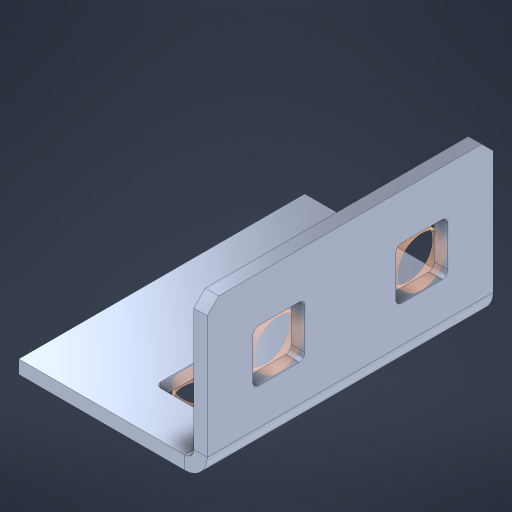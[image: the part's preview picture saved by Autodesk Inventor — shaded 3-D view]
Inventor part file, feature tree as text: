
AUTODESK INVENTOR PART (.ipt)
format: ipt  version: 2023 (Build 270158000, 158)  size: 379,392 bytes
history: native  units: in
note: dims shown in document units (in); Inventor stores cm internally (conversion verified against a paired STEP export)
features: sheet_metal_op x10, other x9, sketch x8, extrude x3, mirror x1, pattern_linear x1, chamfer x1
ambient origin geometry x8: Origin, YZ Plane, XZ Plane, XY Plane, X Axis, Y Axis, Z Axis, Center Point
bodies: Solid1 (feature_tree), Body (feature_tree)
feature tree (33):
  other  "Flange Pattern Plane"
  sheet_metal_op  "Flange Pattern"
  sheet_metal_op  "Body Pattern"
  other  "Arc Length"
  mirror  "Notch Mirror"
  pattern_linear  "Notch Pattern"  Spacing1=0.1875in  [1 undecoded]
  chamfer  "End Chamfer"
  extrude  "Half Cut"  Depth=0.0469in
  sketch  "Sketch1"  dims[d0=2.5in]
  other  "Plate1"
  sketch  "Sketch2"  dims[d1=1.0in]
  other  "Plate2"
  sheet_metal_op  "Bend1"
  sheet_metal_op  "Corner1"
  sketch  "Sketch3"  dims[d2=0.0469in]
  other  "Flange Pattern Sketch"
  sketch  "Sketch7"  dims[d3=0.0469in]
  other  "Srf1"
  other  "Srf2"
  sketch  "Sketch8"  dims[d4=0.0234in]
  sketch  "Sketch9"  dims[d5=0.0938in]
  other  "Srf91"
  sheet_metal_op  "Body Pattern Sketch"
  other  "Srf92"
  sketch  "Sketch13"  dims[d6=0.0469in]
  sketch  "Sketch14"  dims[d7=0.5in d8=90.0deg d9=0.0312in d10=0.1875in d11=0.0469in d12=0.0469in d16=0.182in d17=0.02in d18=0.0469in d19=0.0in d20=0.25in d21=0.25in d46=0.172in d47=1.0in d48=0.0in d49=0.182in d50=0.02in d51=0.25in d52=0.25in d53=0.0469in d54=0.0in d55=0.172in d56=1.0in d57=0.0in d60=0.7874in d62=0.5in d63=0.3937in d65=0.5in d85=0.1227in d86=0.1659in d88=0.04in d89=0.0469in d90=0.0in d91=0.04in d92=0.0491in d95=2.5in d96=0.04in d97=0.25in d98=45.0deg d101=0.0in d102=2.497in d131=0.5in d132=0.7874in d134=0.5in d139=0.5in]
  sheet_metal_op  "Flange Stamp"
  sheet_metal_op  "Flange Circle"
  sheet_metal_op  "Body Stamp"
  sheet_metal_op  "Body Circle"
  sheet_metal_op  "Notch"
  extrude  "ExtrusionSrf2"  Depth=0.0469in
  extrude  "ExtrusionSrf92"  Depth=0.182in
note: 1 required parameter value undecoded (feature->parameter linkage not recoverable at this tier; creation-order binding heuristic only, values carry confidence <= 0.55)
